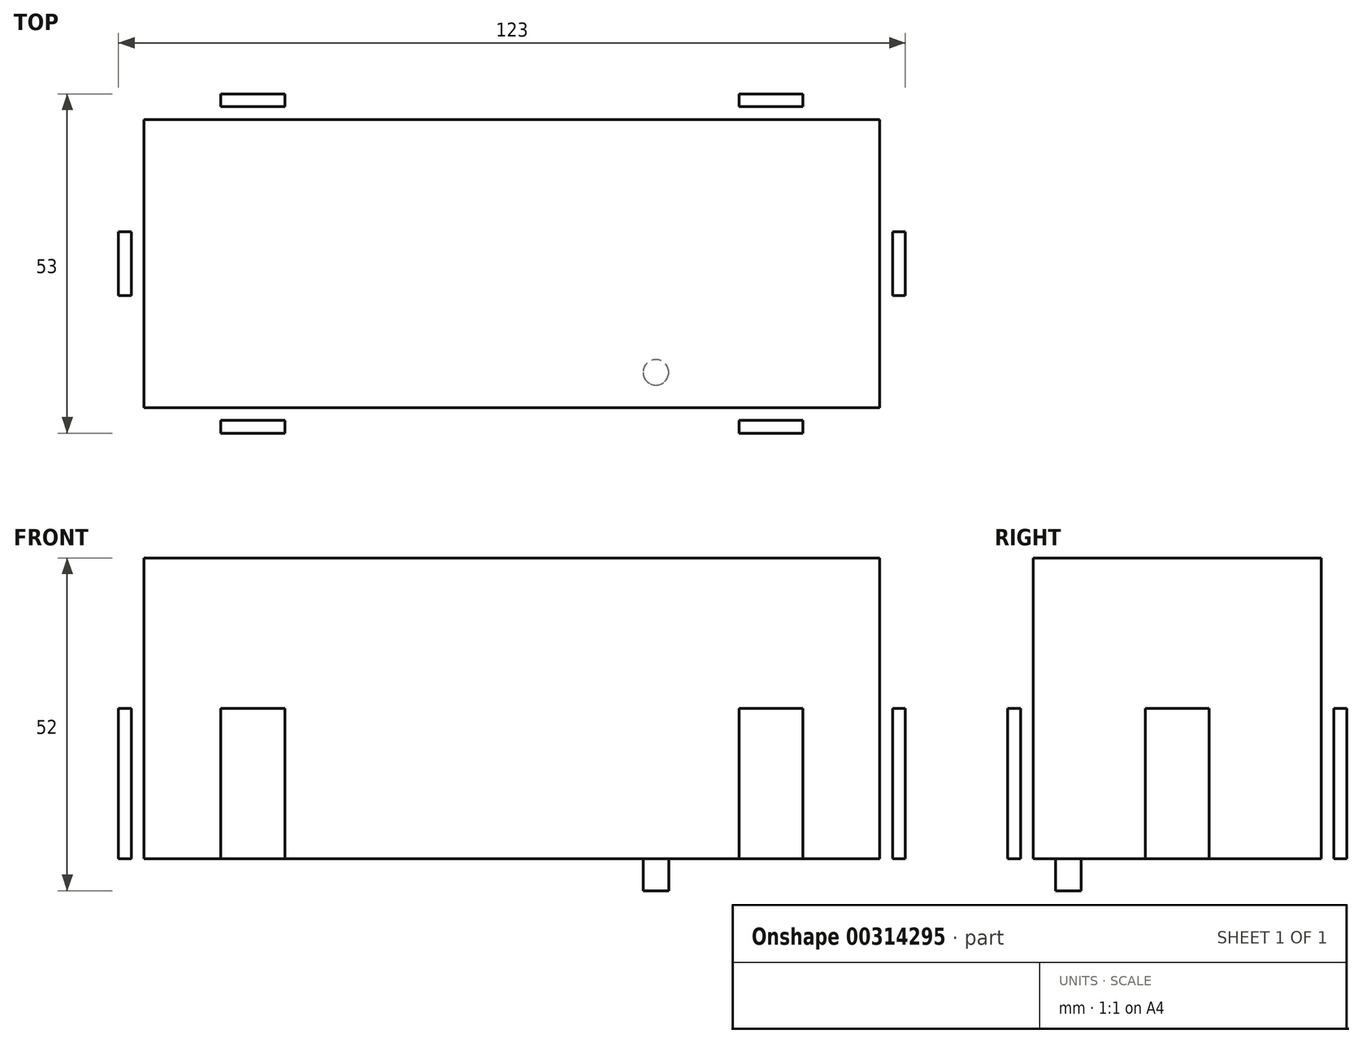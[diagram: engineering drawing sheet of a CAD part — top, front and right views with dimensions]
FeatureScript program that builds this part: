
annotation { "Feature Type Name" : "Feature", "Feature Type Description" : "" }
export const myFeature = defineFeature(function(context is Context, id is Id, definition is map)
    precondition{}
    {
        {
            var Q0;
            Q0=qCreatedBy(makeId("Top.planeOp"),FACE);
            var sketch = newSketch(context, id + "F0", { "sketchPlane" : qUnion([Q0])});
            skLineSegment(sketch, "E0.bottom", {"start": v(0, 0) * mm, "end": v(115, 0) * mm});
            skLineSegment(sketch, "E0.top", {"start": v(0, -45) * mm, "end": v(115, -45) * mm});
            skLineSegment(sketch, "E0.left", {"start": v(0, 0) * mm, "end": v(0, -45) * mm});
            skLineSegment(sketch, "E0.right", {"start": v(115, 0) * mm, "end": v(115, -45) * mm});
            skSolve(sketch);
        }
        {
            var Q0;
            Q0 = qSketchRegion(id + "F0", true);
            extrude(context, id + "F1", {"entities" : qUnion([Q0]), "depth" : 47 * mm});
        }
        {
            var Q0;
            Q0=qCreatedBy(makeId("Top.planeOp"),FACE);
            var sketch = newSketch(context, id + "F2", { "sketchPlane" : qUnion([Q0])});
            skLineSegment(sketch, "E1.bottom", {"start": v(-4, 4) * mm, "end": v(119, 4) * mm});
            skLineSegment(sketch, "E1.top", {"start": v(-4, -49) * mm, "end": v(119, -49) * mm});
            skLineSegment(sketch, "E1.left", {"start": v(-4, 4) * mm, "end": v(-4, -49) * mm});
            skLineSegment(sketch, "E1.right", {"start": v(119, 4) * mm, "end": v(119, -49) * mm});
            skLineSegment(sketch, "E2", {"start": v(112.9, 0) * mm, "end": v(112.9, 4) * mm, "construction": true});
            skLineSegment(sketch, "E3", {"start": v(114.02, -49) * mm, "end": v(114.02, -45) * mm, "construction": true});
            skLineSegment(sketch, "E4", {"start": v(115, -22.5) * mm, "end": v(119, -22.5) * mm, "construction": true});
            skLineSegment(sketch, "E5", {"start": v(-4, -21.85) * mm, "end": v(0, -21.85) * mm, "construction": true});
            skPoint(sketch, "E6", {"position": v(119, -22.5) * mm});
            skSolve(sketch);
        }
        {
            var Q0;
            Q0 = qSketchRegion(id + "F2", true);
            extrude(context, id + "F3", {"entities" : qUnion([Q0]), "oppositeDirection" : true, "depth" : 5 * mm});
        }
        {
            var Q0;
            Q0=makeQuery(id+"F3.opExtrude","CAP_FACE",FACE,{"disambiguationData":[OSD([sQuery(id+"F2.wireOp",EDGE,"E1.bottom"),sQuery(id+"F2.wireOp",EDGE,"E1.top"),sQuery(id+"F2.wireOp",EDGE,"E1.left"),sQuery(id+"F2.wireOp",EDGE,"E1.right")])],"isStart":true});
            var sketch = newSketch(context, id + "F4", { "sketchPlane" : qUnion([Q0])});
            skLineSegment(sketch, "E7.0", {"start": v(-4, 4) * mm, "end": v(119, 4) * mm});
            skLineSegment(sketch, "E8.0", {"start": v(119, 4) * mm, "end": v(119, -49) * mm});
            skLineSegment(sketch, "E9.0", {"start": v(-4, 4) * mm, "end": v(-4, -49) * mm});
            skLineSegment(sketch, "E10.0", {"start": v(-4, -49) * mm, "end": v(119, -49) * mm});
            skLineSegment(sketch, "E11.bottom", {"start": v(11.09, 28.37) * mm, "end": v(20, 28.37) * mm});
            skLineSegment(sketch, "E11.top", {"start": v(11.09, 26.28) * mm, "end": v(20, 26.28) * mm});
            skLineSegment(sketch, "E11.left", {"start": v(11.09, 28.37) * mm, "end": v(11.09, 26.28) * mm});
            skLineSegment(sketch, "E11.right", {"start": v(20, 28.37) * mm, "end": v(20, 26.28) * mm});
            skLineSegment(sketch, "E12.bottom", {"start": v(-2, 2) * mm, "end": v(117, 2) * mm});
            skLineSegment(sketch, "E12.top", {"start": v(-2, -47) * mm, "end": v(117, -47) * mm});
            skLineSegment(sketch, "E12.left", {"start": v(-2, 2) * mm, "end": v(-2, -47) * mm});
            skLineSegment(sketch, "E12.right", {"start": v(117, 2) * mm, "end": v(117, -47) * mm});
            skLineSegment(sketch, "E13", {"start": v(12, 4) * mm, "end": v(12, -49) * mm});
            skLineSegment(sketch, "E14", {"start": v(22, 4) * mm, "end": v(22, -49) * mm});
            skLineSegment(sketch, "E15", {"start": v(93, 4) * mm, "end": v(93, -49) * mm});
            skLineSegment(sketch, "E16", {"start": v(103, 4) * mm, "end": v(103, -49) * mm});
            skLineSegment(sketch, "E17", {"start": v(12, -14.4) * mm, "end": v(22, -14.4) * mm, "construction": true});
            skLineSegment(sketch, "E18", {"start": v(93, -17.68) * mm, "end": v(103, -17.68) * mm, "construction": true});
            skLineSegment(sketch, "E19", {"start": v(-4, -9.95) * mm, "end": v(12, -9.95) * mm, "construction": true});
            skLineSegment(sketch, "E20", {"start": v(103, -12.08) * mm, "end": v(119, -12.08) * mm, "construction": true});
            skLineSegment(sketch, "E21", {"start": v(-4, -17.5) * mm, "end": v(119, -17.5) * mm});
            skLineSegment(sketch, "E22", {"start": v(-4, -27.5) * mm, "end": v(119, -27.5) * mm});
            skLineSegment(sketch, "E23", {"start": v(60.65, -17.5) * mm, "end": v(60.65, -27.5) * mm, "construction": true});
            skLineSegment(sketch, "E24", {"start": v(73.6, 4) * mm, "end": v(73.6, -17.5) * mm, "construction": true});
            skLineSegment(sketch, "E25", {"start": v(74.56, -27.5) * mm, "end": v(74.56, -49) * mm, "construction": true});
            skSolve(sketch);
        }
        {
            var Q0;
            {var subQ0=sQuery(id+"F4.wireOp",EDGE,"E13");var subQ1=sQuery(id+"F4.wireOp",EDGE,"E7.0");var subQ2=makeQuery(id+"F4.imprint","INTERSECT",VERTEX,{"derivedFrom":[subQ1,subQ0]});Q0=makeQuery(id+"F4.imprint","IMPRINT",FACE,{"disambiguationData":[TD([[makeQuery(id+"F4.imprint","IMPRINT",EDGE,{"disambiguationData":[TD([[subQ2,-1.0]])],"derivedFrom":subQ1}),-1.0]])]});}
            var Q1;
            {var subQ0=sQuery(id+"F4.wireOp",EDGE,"E21");var subQ1=sQuery(id+"F4.wireOp",EDGE,"E9.0");var subQ2=makeQuery(id+"F4.imprint","INTERSECT",VERTEX,{"derivedFrom":[subQ1,subQ0]});Q1=makeQuery(id+"F4.imprint","IMPRINT",FACE,{"disambiguationData":[TD([[makeQuery(id+"F4.imprint","IMPRINT",EDGE,{"disambiguationData":[TD([[subQ2,-1.0]])],"derivedFrom":subQ1}),1.0]])]});}
            var Q2;
            {var subQ0=sQuery(id+"F4.wireOp",EDGE,"E13");var subQ1=sQuery(id+"F4.wireOp",EDGE,"E10.0");var subQ2=makeQuery(id+"F4.imprint","INTERSECT",VERTEX,{"derivedFrom":[subQ1,subQ0]});Q2=makeQuery(id+"F4.imprint","IMPRINT",FACE,{"disambiguationData":[TD([[makeQuery(id+"F4.imprint","IMPRINT",EDGE,{"disambiguationData":[TD([[subQ2,-1.0]])],"derivedFrom":subQ1}),1.0]])]});}
            var Q3;
            {var subQ0=sQuery(id+"F4.wireOp",EDGE,"E15");var subQ1=sQuery(id+"F4.wireOp",EDGE,"E10.0");var subQ2=makeQuery(id+"F4.imprint","INTERSECT",VERTEX,{"derivedFrom":[subQ1,subQ0]});Q3=makeQuery(id+"F4.imprint","IMPRINT",FACE,{"disambiguationData":[TD([[makeQuery(id+"F4.imprint","IMPRINT",EDGE,{"disambiguationData":[TD([[subQ2,-1.0]])],"derivedFrom":subQ1}),1.0]])]});}
            var Q4;
            {var subQ0=sQuery(id+"F4.wireOp",EDGE,"E15");var subQ1=sQuery(id+"F4.wireOp",EDGE,"E7.0");var subQ2=makeQuery(id+"F4.imprint","INTERSECT",VERTEX,{"derivedFrom":[subQ1,subQ0]});Q4=makeQuery(id+"F4.imprint","IMPRINT",FACE,{"disambiguationData":[TD([[makeQuery(id+"F4.imprint","IMPRINT",EDGE,{"disambiguationData":[TD([[subQ2,-1.0]])],"derivedFrom":subQ1}),-1.0]])]});}
            var Q5;
            {var subQ0=sQuery(id+"F4.wireOp",EDGE,"E21");var subQ1=sQuery(id+"F4.wireOp",EDGE,"E8.0");var subQ2=makeQuery(id+"F4.imprint","INTERSECT",VERTEX,{"derivedFrom":[subQ1,subQ0]});Q5=makeQuery(id+"F4.imprint","IMPRINT",FACE,{"disambiguationData":[TD([[makeQuery(id+"F4.imprint","IMPRINT",EDGE,{"disambiguationData":[TD([[subQ2,-1.0]])],"derivedFrom":subQ1}),-1.0]])]});}
            extrude(context, id + "F5", {"entities" : qUnion([Q0, Q1, Q2, Q3, Q4, Q5]), "operationType" : NewBodyOperationType.ADD, "depth" : 23.5 * mm});
        }
        {
            var Q0;
            Q0=makeQuery(id+"F3.opExtrude","CAP_FACE",FACE,{"disambiguationData":[OSD([sQuery(id+"F2.wireOp",EDGE,"E1.bottom"),sQuery(id+"F2.wireOp",EDGE,"E1.top"),sQuery(id+"F2.wireOp",EDGE,"E1.left"),sQuery(id+"F2.wireOp",EDGE,"E1.right")])],"isStart":false});
            var sketch = newSketch(context, id + "F6", { "sketchPlane" : qUnion([Q0])});
            skLineSegment(sketch, "E26.bottom", {"start": v(-14.63, 72.02) * mm, "end": v(6.59, 72.02) * mm});
            skLineSegment(sketch, "E26.top", {"start": v(-14.63, 53.02) * mm, "end": v(6.59, 53.02) * mm});
            skLineSegment(sketch, "E26.left", {"start": v(-14.63, 72.02) * mm, "end": v(-14.63, 53.02) * mm});
            skLineSegment(sketch, "E26.right", {"start": v(6.59, 72.02) * mm, "end": v(6.59, 53.02) * mm});
            skSolve(sketch);
        }
        {
            var Q0;
            Q0=makeQuery(id+"F6.imprint","IMPRINT",FACE,{"disambiguationData":[TD([[makeQuery(id+"F6.imprint","IMPRINT",EDGE,{"derivedFrom":makeQuery(id+"F3.opExtrude","CAP_EDGE",EDGE,{"disambiguationData":[OSD([sQuery(id+"F2.wireOp",EDGE,"E1.bottom")])],"isStart":false})}),1.0]])]});
            var sketch = newSketch(context, id + "F7", { "sketchPlane" : qUnion([Q0])});
            skPoint(sketch, "E27.0", {"position": v(57.5, 49) * mm});
            skLineSegment(sketch, "E28", {"start": v(57.5, 49) * mm, "end": v(57.5, -4) * mm, "construction": true});
            skLineSegment(sketch, "E29", {"start": v(57.5, 39.5) * mm, "end": v(-4.43, 39.5) * mm, "construction": true});
            skLineSegment(sketch, "E30", {"start": v(29, 49) * mm, "end": v(29, -4.14) * mm, "construction": true});
            skCircle(sketch, "E31", {"center": v(35, 39.5) * mm, "radius": 2 * mm});
            skCircle(sketch, "E32.MirrorC", {"center": v(80, 39.5) * mm, "radius": 2 * mm});
            skSolve(sketch);
        }
        {
            var Q0;
            Q0=makeQuery(id+"F7.imprint","IMPRINT",FACE,{"disambiguationData":[TD([[makeQuery(id+"F7.imprint","IMPRINT",EDGE,{"derivedFrom":sQuery(id+"F7.wireOp",EDGE,"E32.MirrorC")}),-1.0]])]});
            var Q1;
            Q1=makeQuery(id+"F7.imprint","IMPRINT",FACE,{"disambiguationData":[TD([[makeQuery(id+"F7.imprint","IMPRINT",EDGE,{"derivedFrom":sQuery(id+"F7.wireOp",EDGE,"E31")}),1.0]])]});
            var Q2;
            Q2=makeQuery(id+"F3.opExtrude","CAP_FACE",FACE,{"disambiguationData":[OSD([sQuery(id+"F2.wireOp",EDGE,"E1.bottom"),sQuery(id+"F2.wireOp",EDGE,"E1.top"),sQuery(id+"F2.wireOp",EDGE,"E1.left"),sQuery(id+"F2.wireOp",EDGE,"E1.right")])],"isStart":true});
            extrude(context, id + "F8", {"entities" : qUnion([Q0, Q1]), "operationType" : NewBodyOperationType.REMOVE, "endBound" : BoundingType.UP_TO_SURFACE, "oppositeDirection" : true, "endBoundEntityFace" : qUnion([Q2]), "depth" : 25 * mm});
        }
    });
